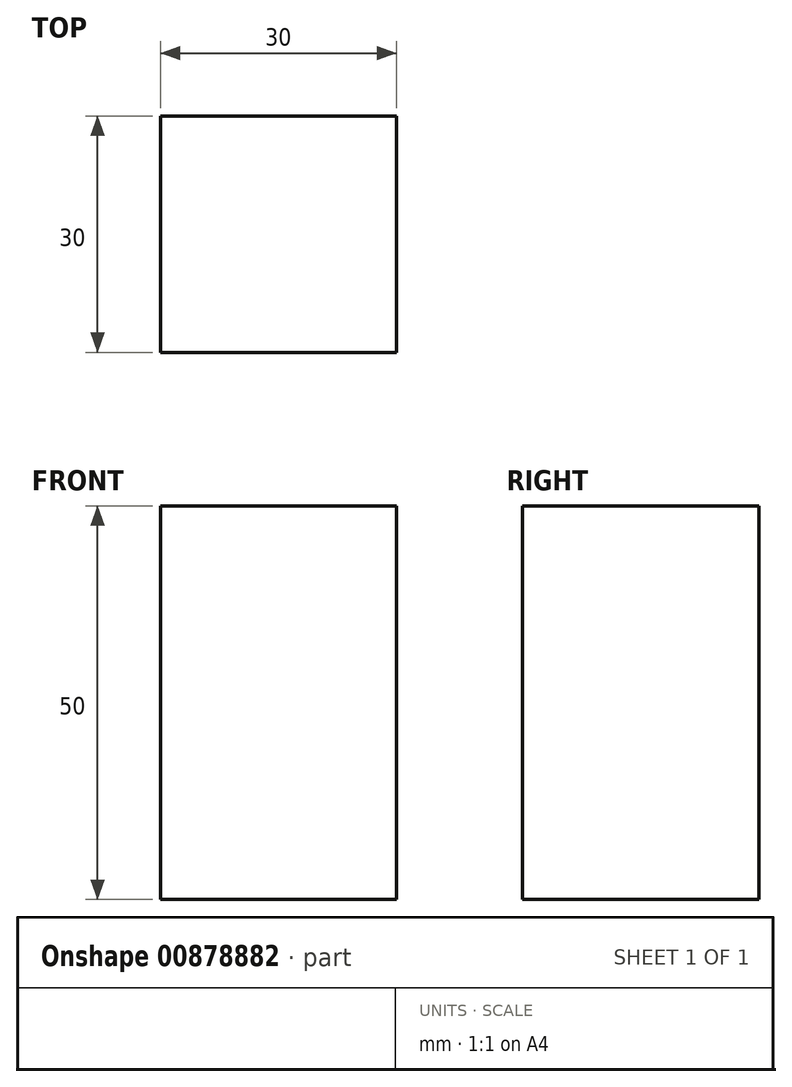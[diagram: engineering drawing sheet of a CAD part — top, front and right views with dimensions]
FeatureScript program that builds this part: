
annotation { "Feature Type Name" : "Feature", "Feature Type Description" : "" }
export const myFeature = defineFeature(function(context is Context, id is Id, definition is map)
    precondition{}
    {
        {
            var Q0;
            Q0=qCreatedBy(makeId("Top.planeOp"),FACE);
            var sketch = newSketch(context, id + "F0", { "sketchPlane" : qUnion([Q0])});
            skLineSegment(sketch, "E0.bottom", {"start": v(15, -15) * mm, "end": v(-15, -15) * mm});
            skLineSegment(sketch, "E0.top", {"start": v(15, 15) * mm, "end": v(-15, 15) * mm});
            skLineSegment(sketch, "E0.left", {"start": v(15, -15) * mm, "end": v(15, 15) * mm});
            skLineSegment(sketch, "E0.right", {"start": v(-15, -15) * mm, "end": v(-15, 15) * mm});
            skPoint(sketch, "E0.middle", {"position": v(0, 0) * mm});
            skSolve(sketch);
        }
        {
            var Q0;
            Q0=qCreatedBy(makeId("Front.planeOp"),FACE);
            var sketch = newSketch(context, id + "F1", { "sketchPlane" : qUnion([Q0])});
            skLineSegment(sketch, "E1", {"start": v(0, 0) * mm, "end": v(0, 50) * mm});
            skSolve(sketch);
        }
        {
            var Q0;
            Q0=makeQuery(id+"F0.imprint","IMPRINT",FACE,{"disambiguationData":[TD([[makeQuery(id+"F0.imprint","IMPRINT",EDGE,{"derivedFrom":sQuery(id+"F0.wireOp",EDGE,"E0.bottom")}),-1.0]])]});
            var Q1;
            Q1=sQuery(id+"F1.wireOp",EDGE,"E1");
            sweep(context, id + "F2", {"profiles" : qUnion([Q0]), "path" : qUnion([Q1])});
        }
    });
